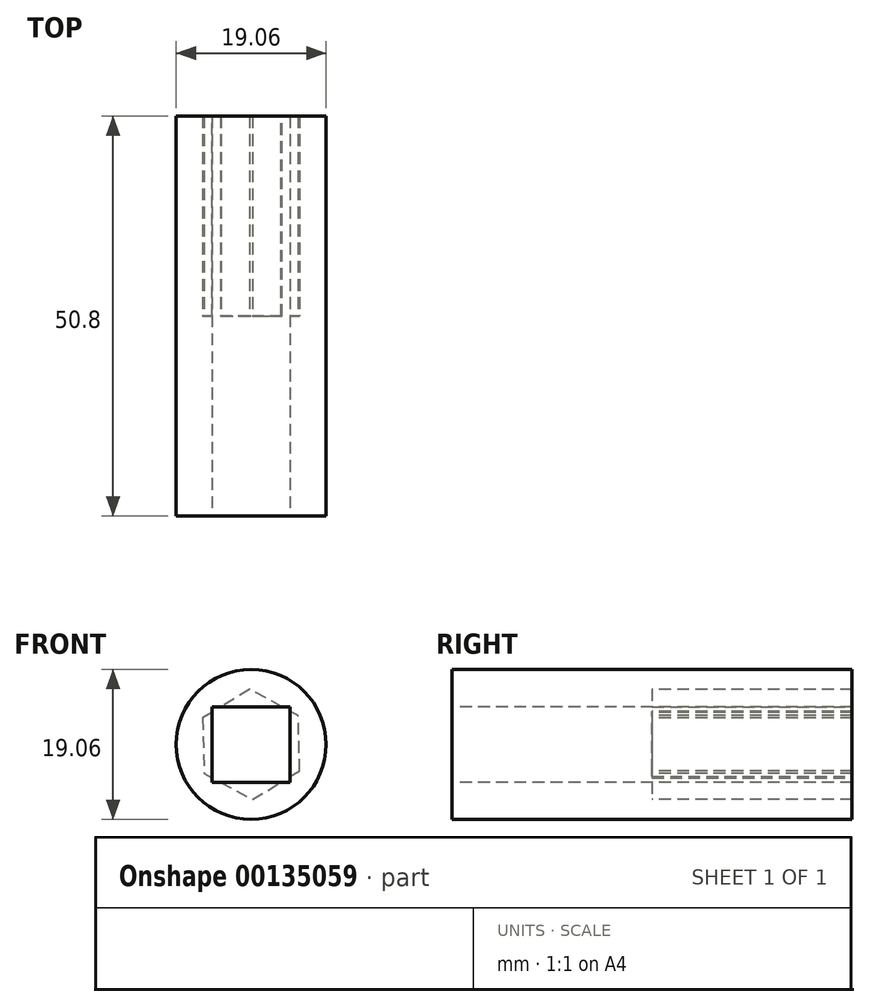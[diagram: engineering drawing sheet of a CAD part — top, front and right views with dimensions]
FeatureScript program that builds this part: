
annotation { "Feature Type Name" : "Feature", "Feature Type Description" : "" }
export const myFeature = defineFeature(function(context is Context, id is Id, definition is map)
    precondition{}
    {
        {
            var Q0;
            Q0=qCreatedBy(makeId("Front.planeOp"),FACE);
            var sketch = newSketch(context, id + "F0", { "sketchPlane" : qUnion([Q0])});
            skCircle(sketch, "E0", {"center": v(0, 0) * mm, "radius": 9.53 * mm});
            skSolve(sketch);
        }
        {
            var Q0;
            Q0 = qSketchRegion(id + "F0", true);
            extrude(context, id + "F1", {"entities" : qUnion([Q0]), "depth" : 25.4 * mm});
        }
        {
            var Q0;
            Q0=qCreatedBy(makeId("Front.planeOp"),FACE);
            var sketch = newSketch(context, id + "F2", { "sketchPlane" : qUnion([Q0])});
            skLineSegment(sketch, "E1.bottom", {"start": v(4.76, -4.76) * mm, "end": v(-4.76, -4.76) * mm});
            skLineSegment(sketch, "E1.top", {"start": v(4.76, 4.76) * mm, "end": v(-4.76, 4.76) * mm});
            skLineSegment(sketch, "E1.left", {"start": v(4.76, -4.76) * mm, "end": v(4.76, 4.76) * mm});
            skLineSegment(sketch, "E1.right", {"start": v(-4.76, -4.76) * mm, "end": v(-4.76, 4.76) * mm});
            skPoint(sketch, "E1.middle", {"position": v(0, 0) * mm});
            skCircle(sketch, "E2", {"center": v(0, 0) * mm, "radius": 4.76 * mm});
            skSolve(sketch);
        }
        {
            var Q0;
            {var subQ0=sQuery(id+"F2.wireOp",EDGE,"E2");var subQ1=makeQuery(id+"F2.imprint","INTERSECT",VERTEX,{"derivedFrom":[sQuery(id+"F2.wireOp",EDGE,"E1.top"),subQ0]});Q0=makeQuery(id+"F2.imprint","IMPRINT",FACE,{"disambiguationData":[TD([[makeQuery(id+"F2.imprint","IMPRINT",EDGE,{"disambiguationData":[TD([[subQ1,1.0]])],"derivedFrom":subQ0}),1.0]])]});}
            extrude(context, id + "F3", {"entities" : qUnion([Q0]), "operationType" : NewBodyOperationType.REMOVE, "endBound" : BoundingType.THROUGH_ALL, "depth" : 25.4 * mm});
        }
        {
            var Q0;
            Q0=makeQuery(id+"F1.opExtrude","CAP_FACE",FACE,{"disambiguationData":[OSD([sQuery(id+"F0.wireOp",EDGE,"E0")])],"isStart":true});
            var sketch = newSketch(context, id + "F4", { "sketchPlane" : qUnion([Q0])});
            skCircle(sketch, "E3.cCircle", {"center": v(0, 0) * mm, "radius": 6.07 * mm, "construction": true});
            skLineSegment(sketch, "E3.0", {"start": v(0.18, 7.01) * mm, "end": v(6.16, 3.35) * mm});
            skLineSegment(sketch, "E3.1", {"start": v(6.16, 3.35) * mm, "end": v(5.98, -3.66) * mm});
            skLineSegment(sketch, "E3.2", {"start": v(5.98, -3.66) * mm, "end": v(-0.18, -7.01) * mm});
            skLineSegment(sketch, "E3.3", {"start": v(-0.18, -7.01) * mm, "end": v(-6.16, -3.35) * mm});
            skLineSegment(sketch, "E3.4", {"start": v(-6.16, -3.35) * mm, "end": v(-5.98, 3.66) * mm});
            skLineSegment(sketch, "E3.5", {"start": v(-5.98, 3.66) * mm, "end": v(0.18, 7.01) * mm});
            skPoint(sketch, "E3.0.midPoint", {"position": v(3.17, 5.18) * mm});
            skSolve(sketch);
        }
        {
            var Q0;
            Q0=makeQuery(id+"F4.imprint","IMPRINT",FACE,{"disambiguationData":[TD([[makeQuery(id+"F4.imprint","IMPRINT",EDGE,{"derivedFrom":sQuery(id+"F4.wireOp",EDGE,"E3.0")}),1.0]])]});
            extrude(context, id + "F5", {"entities" : qUnion([Q0]), "operationType" : NewBodyOperationType.ADD, "depth" : 25.4 * mm});
        }
        {
            var Q0;
            Q0=makeQuery(id+"F1.opExtrude","CAP_FACE",FACE,{"disambiguationData":[OSD([sQuery(id+"F0.wireOp",EDGE,"E0")])],"isStart":false});
            var sketch = newSketch(context, id + "F6", { "sketchPlane" : qUnion([Q0])});
            skLineSegment(sketch, "E4.bottom", {"start": v(-4.96, 4.8) * mm, "end": v(4.96, 4.8) * mm});
            skLineSegment(sketch, "E4.top", {"start": v(-4.96, -4.8) * mm, "end": v(4.96, -4.8) * mm});
            skLineSegment(sketch, "E4.left", {"start": v(-4.96, 4.8) * mm, "end": v(-4.96, -4.8) * mm});
            skLineSegment(sketch, "E4.right", {"start": v(4.96, 4.8) * mm, "end": v(4.96, -4.8) * mm});
            skPoint(sketch, "E4.middle", {"position": v(0, 0) * mm});
            skSolve(sketch);
        }
        {
            var Q0;
            Q0 = qSketchRegion(id + "F6", true);
            extrude(context, id + "F7", {"entities" : qUnion([Q0]), "operationType" : NewBodyOperationType.REMOVE, "endBound" : BoundingType.THROUGH_ALL, "oppositeDirection" : true, "depth" : 25.4 * mm});
        }
    });
